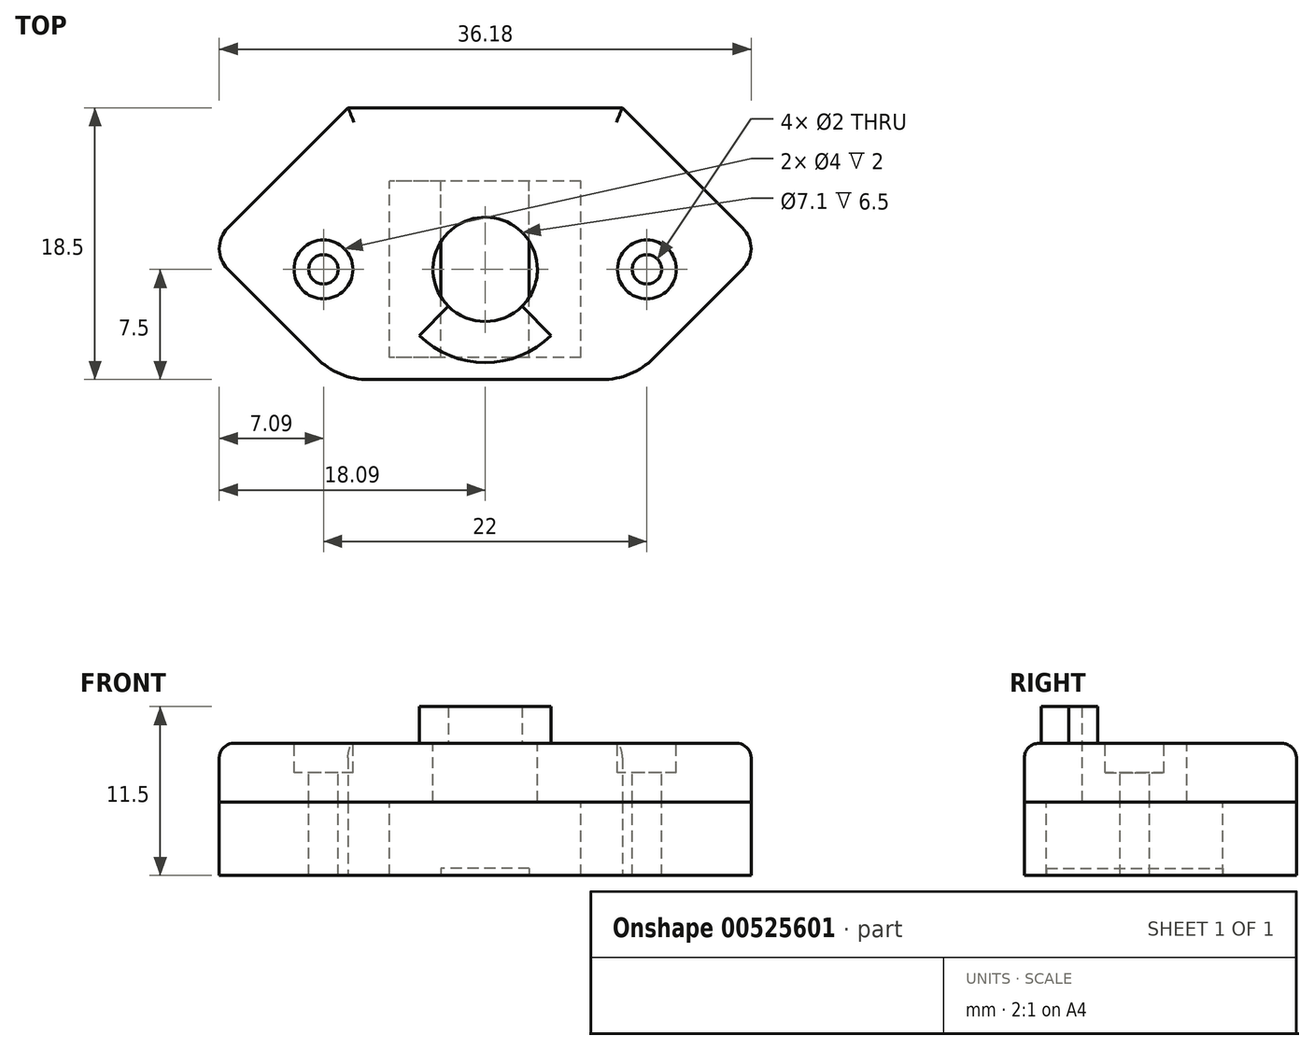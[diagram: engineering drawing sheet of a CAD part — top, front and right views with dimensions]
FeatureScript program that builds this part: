
annotation { "Feature Type Name" : "Feature", "Feature Type Description" : "" }
export const myFeature = defineFeature(function(context is Context, id is Id, definition is map)
    precondition{}
    {
        {
            var Q0;
            Q0=qCreatedBy(makeId("Top.planeOp"),FACE);
            var sketch = newSketch(context, id + "F0", { "sketchPlane" : qUnion([Q0])});
            skLineSegment(sketch, "E0.top", {"start": v(10, 15) * mm, "end": v(-10, 15) * mm});
            skLineSegment(sketch, "E0.left", {"start": v(10, 0) * mm, "end": v(10, 15) * mm});
            skLineSegment(sketch, "E0.right", {"start": v(-10, 0) * mm, "end": v(-10, 15) * mm});
            skPoint(sketch, "E0.middle", {"position": v(0, 7.5) * mm});
            skLineSegment(sketch, "E1", {"start": v(-10, 0) * mm, "end": v(10, 0) * mm});
            skLineSegment(sketch, "E2", {"start": v(0, 7.5) * mm, "end": v(-25.69, 7.5) * mm, "construction": true});
            skArc(sketch, "E3", {"start": v(-17.5, 7.5) * mm, "mid": v(-15.3, 2.2) * mm, "end": v(-10, 0) * mm, "construction": true});
            skLineSegment(sketch, "E4", {"start": v(-10, 0) * mm, "end": v(-17.5, 7.5) * mm});
            skLineSegment(sketch, "E5", {"start": v(-17.5, 7.5) * mm, "end": v(-10, 15) * mm});
            skLineSegment(sketch, "E6", {"start": v(-10, 15) * mm, "end": v(-6.5, 18.5) * mm});
            skLineSegment(sketch, "E7", {"start": v(-6.5, 18.5) * mm, "end": v(6.5, 18.5) * mm});
            skLineSegment(sketch, "E8", {"start": v(10, 0) * mm, "end": v(17.5, 7.5) * mm});
            skLineSegment(sketch, "E9", {"start": v(10, 15) * mm, "end": v(17.5, 7.5) * mm});
            skLineSegment(sketch, "E10", {"start": v(10, 15) * mm, "end": v(6.5, 18.5) * mm});
            skLineSegment(sketch, "E11", {"start": v(-17.5, 7.5) * mm, "end": v(-18.91, 8.91) * mm});
            skLineSegment(sketch, "E12", {"start": v(-18.91, 8.91) * mm, "end": v(-9.33, 18.5) * mm});
            skLineSegment(sketch, "E13", {"start": v(-9.33, 18.5) * mm, "end": v(-6.5, 18.5) * mm});
            skLineSegment(sketch, "E14", {"start": v(17.5, 7.5) * mm, "end": v(18.91, 8.91) * mm});
            skLineSegment(sketch, "E15", {"start": v(18.91, 8.91) * mm, "end": v(9.33, 18.5) * mm});
            skLineSegment(sketch, "E16", {"start": v(9.33, 18.5) * mm, "end": v(6.5, 18.5) * mm});
            skSolve(sketch);
        }
        {
            var Q0;
            Q0=qSketchRegion(id+"F0",true);
            extrude(context, id + "F1", {"entities" : qUnion([Q0]), "depth" : 5 * mm, "offsetDistance" : 25 * mm});
        }
        {
            var Q0;
            Q0=makeQuery(id+"F1.opExtrude","CAP_FACE",FACE,{"disambiguationData":[OSD([sQuery(id+"F0.wireOp",EDGE,"E1"),sQuery(id+"F0.wireOp",EDGE,"E4"),sQuery(id+"F0.wireOp",EDGE,"E5"),sQuery(id+"F0.wireOp",EDGE,"E6"),sQuery(id+"F0.wireOp",EDGE,"E7"),sQuery(id+"F0.wireOp",EDGE,"E8"),sQuery(id+"F0.wireOp",EDGE,"E9"),sQuery(id+"F0.wireOp",EDGE,"E10")])],"isStart":false});
            var sketch = newSketch(context, id + "F2", { "sketchPlane" : qUnion([Q0])});
            skCircle(sketch, "E17", {"center": v(-11, 7.5) * mm, "radius": 1 * mm});
            skCircle(sketch, "E18", {"center": v(11, 7.5) * mm, "radius": 1 * mm});
            skCircle(sketch, "E19", {"center": v(0, 7.5) * mm, "radius": 3.55 * mm, "construction": true});
            skLineSegment(sketch, "E20.bottom", {"start": v(6.5, 1.5) * mm, "end": v(-6.5, 1.5) * mm});
            skLineSegment(sketch, "E20.top", {"start": v(6.5, 13.5) * mm, "end": v(-6.5, 13.5) * mm});
            skLineSegment(sketch, "E20.left", {"start": v(6.5, 1.5) * mm, "end": v(6.5, 13.5) * mm});
            skLineSegment(sketch, "E20.right", {"start": v(-6.5, 1.5) * mm, "end": v(-6.5, 13.5) * mm});
            skSolve(sketch);
        }
        {
            var Q0;
            Q0=qSketchRegion(id+"F2",true);
            extrude(context, id + "F3", {"entities" : qUnion([Q0]), "operationType" : NewBodyOperationType.REMOVE, "oppositeDirection" : true, "offsetDistance" : 25 * mm, "depth" : 5 * mm});
        }
        {
            var Q0;
            Q0=makeQuery(id+"F1.opExtrude","CAP_FACE",FACE,{"disambiguationData":[OSD([sQuery(id+"F0.wireOp",EDGE,"E0.top"),sQuery(id+"F0.wireOp",EDGE,"6JZFKnFd-4U4Z-A5hn-TgZ8-hM0N97EqA9dV"),sQuery(id+"F0.wireOp",EDGE,"Ptp1BsVZ-AEQ3-b6oq-Bfdl-BXNrkdz5Nnmn"),sQuery(id+"F0.wireOp",EDGE,"E1")])],"isStart":true});
            var sketch = newSketch(context, id + "F4", { "sketchPlane" : qUnion([Q0])});
            skPoint(sketch, "E21.middle.positionSnap0", {"position": v(0, -13.5) * mm});
            skPoint(sketch, "E21.centerSnap0", {"position": v(0, -13.5) * mm});
            skLineSegment(sketch, "E22.bottom", {"start": v(3, -1.5) * mm, "end": v(-3, -1.5) * mm});
            skLineSegment(sketch, "E22.top", {"start": v(3, -13.5) * mm, "end": v(-3, -13.5) * mm});
            skLineSegment(sketch, "E22.left", {"start": v(3, -1.5) * mm, "end": v(3, -13.5) * mm});
            skLineSegment(sketch, "E22.right", {"start": v(-3, -1.5) * mm, "end": v(-3, -13.5) * mm});
            skPoint(sketch, "E22.middle", {"position": v(0, -7.5) * mm});
            skPoint(sketch, "E22.middle.positionSnap0", {"position": v(6.5, -7.5) * mm});
            skPoint(sketch, "E22.centerSnap0", {"position": v(6.5, -7.5) * mm});
            skSolve(sketch);
        }
        {
            var Q0;
            Q0 = qSketchRegion(id + "F4", true);
            extrude(context, id + "F5", {"entities" : qUnion([Q0]), "operationType" : NewBodyOperationType.ADD, "oppositeDirection" : true, "depth" : 0.5 * mm, "offsetDistance" : 25 * mm});
        }
        {
            var Q0;
            Q0=makeQuery(id+"F1.opExtrude","CAP_FACE",FACE,{"disambiguationData":[OSD([sQuery(id+"F0.wireOp",EDGE,"E0.top"),sQuery(id+"F0.wireOp",EDGE,"6JZFKnFd-4U4Z-A5hn-TgZ8-hM0N97EqA9dV"),sQuery(id+"F0.wireOp",EDGE,"Ptp1BsVZ-AEQ3-b6oq-Bfdl-BXNrkdz5Nnmn"),sQuery(id+"F0.wireOp",EDGE,"E1")])],"isStart":false});
            var sketch = newSketch(context, id + "F6", { "sketchPlane" : qUnion([Q0])});
            skLineSegment(sketch, "E23", {"start": v(-10, 0) * mm, "end": v(-18.91, 8.91) * mm});
            skLineSegment(sketch, "E24", {"start": v(-18.91, 8.91) * mm, "end": v(-9.33, 18.5) * mm});
            skLineSegment(sketch, "E25", {"start": v(-9.33, 18.5) * mm, "end": v(9.33, 18.5) * mm});
            skLineSegment(sketch, "E26", {"start": v(9.33, 18.5) * mm, "end": v(18.91, 8.91) * mm});
            skLineSegment(sketch, "E27", {"start": v(18.91, 8.91) * mm, "end": v(10, 0) * mm});
            skLineSegment(sketch, "E28", {"start": v(10, 0) * mm, "end": v(-10, 0) * mm});
            skSolve(sketch);
        }
        {
            var Q0;
            Q0 = qSketchRegion(id + "F6", true);
            extrude(context, id + "F7", {"entities" : qUnion([Q0]), "depth" : 4 * mm, "offsetDistance" : 25 * mm});
        }
        {
            var Q0;
            Q0=makeQuery(id+"F7.opExtrude","CAP_FACE",FACE,{"disambiguationData":[OSD([sQuery(id+"F6.wireOp",EDGE,"E23"),sQuery(id+"F6.wireOp",EDGE,"E24"),sQuery(id+"F6.wireOp",EDGE,"E25"),sQuery(id+"F6.wireOp",EDGE,"E26"),sQuery(id+"F6.wireOp",EDGE,"E27"),sQuery(id+"F6.wireOp",EDGE,"E28")])],"isStart":false});
            var sketch = newSketch(context, id + "F8", { "sketchPlane" : qUnion([Q0])});
            skCircle(sketch, "E29", {"center": v(-11, 7.5) * mm, "radius": 1 * mm, "construction": true});
            skCircle(sketch, "E30", {"center": v(11, 7.5) * mm, "radius": 1 * mm, "construction": true});
            skCircle(sketch, "E31", {"center": v(0, 7.5) * mm, "radius": 3.55 * mm});
            skLineSegment(sketch, "E32", {"start": v(0, 7.5) * mm, "end": v(-2.51, 4.99) * mm, "construction": true});
            skLineSegment(sketch, "E33", {"start": v(0, 7.5) * mm, "end": v(2.08, 7.5) * mm, "construction": true});
            skLineSegment(sketch, "E34", {"start": v(0, 8.49) * mm, "end": v(0, 7.5) * mm, "construction": true});
            skLineSegment(sketch, "E35", {"start": v(0, 7.5) * mm, "end": v(2.51, 4.99) * mm, "construction": true});
            skLineSegment(sketch, "E36", {"start": v(-2.51, 4.99) * mm, "end": v(-3.57, 3.93) * mm, "construction": true});
            skLineSegment(sketch, "E37", {"start": v(2.51, 4.99) * mm, "end": v(3.57, 3.93) * mm, "construction": true});
            skArc(sketch, "E38", {"start": v(-3.57, 3.93) * mm, "mid": v(0, 2.45) * mm, "end": v(3.57, 3.93) * mm, "construction": true});
            skSolve(sketch);
        }
        {
            var Q0;
            Q0 = qSketchRegion(id + "F8", true);
            extrude(context, id + "F9", {"entities" : qUnion([Q0]), "operationType" : NewBodyOperationType.REMOVE, "oppositeDirection" : true, "depth" : 4 * mm, "offsetDistance" : 25 * mm});
        }
        {
            var Q0;
            Q0=makeQuery(id+"F7.opExtrude","CAP_EDGE",EDGE,{"disambiguationData":[OSD([sQuery(id+"F6.wireOp",EDGE,"E23")])],"isStart":false});
            var Q1;
            Q1=makeQuery(id+"F7.opExtrude","CAP_EDGE",EDGE,{"disambiguationData":[OSD([sQuery(id+"F6.wireOp",EDGE,"E28")])],"isStart":false});
            var Q2;
            Q2=makeQuery(id+"F7.opExtrude","CAP_EDGE",EDGE,{"disambiguationData":[OSD([sQuery(id+"F6.wireOp",EDGE,"E27")])],"isStart":false});
            var Q3;
            Q3=makeQuery(id+"F7.opExtrude","CAP_EDGE",EDGE,{"disambiguationData":[OSD([sQuery(id+"F6.wireOp",EDGE,"E26")])],"isStart":false});
            var Q4;
            Q4=makeQuery(id+"F7.opExtrude","CAP_EDGE",EDGE,{"disambiguationData":[OSD([sQuery(id+"F6.wireOp",EDGE,"E25")])],"isStart":false});
            var Q5;
            Q5=makeQuery(id+"F7.opExtrude","CAP_EDGE",EDGE,{"disambiguationData":[OSD([sQuery(id+"F6.wireOp",EDGE,"E24")])],"isStart":false});
            fillet(context, id + "F10", {"entities" : qUnion([Q0, Q1, Q2, Q3, Q4, Q5]), "radius" : 1 * mm, "tangentPropagation" : true, "defaultsChanged" : false, "vertexSettings" : [], "allowEdgeOverflow" : false});
        }
        {
            var Q0;
            Q0=sQuery(id+"F8.wireOp",VERTEX,"E30.center");
            var Q1;
            Q1=sQuery(id+"F8.wireOp",VERTEX,"E29.center");
            var Q2;
            Q2=makeQuery(id+"F7.opExtrude","SWEPT_BODY",BODY,{"disambiguationData":[OSD([sQuery(id+"F6.wireOp",EDGE,"E23"),sQuery(id+"F6.wireOp",EDGE,"E24"),sQuery(id+"F6.wireOp",EDGE,"E25"),sQuery(id+"F6.wireOp",EDGE,"E26"),sQuery(id+"F6.wireOp",EDGE,"E27"),sQuery(id+"F6.wireOp",EDGE,"E28")])]});
            hole(context, id + "F11", {"style" : HoleStyle.C_BORE, "endStyle" : HoleEndStyle.BLIND, "holeDiameter" : 2 * mm, "cBoreDiameter" : 4 * mm, "cBoreDepth" : 2 * mm, "majorDiameter" : 5 * mm, "holeDepth" : 20 * mm, "tappedDepth" : 12 * mm, "tapClearance" : 3, "locations" : qUnion([Q0, Q1]), "scope" : qUnion([Q2])});
        }
        {
            var Q0;
            Q0=makeQuery(id+"F1.opExtrude","SWEPT_EDGE",EDGE,{"disambiguationData":[OSD([sQuery(id+"F0.wireOp",EDGE,"E0.right"),sQuery(id+"F0.wireOp",EDGE,"E1"),sQuery(id+"F0.wireOp",EDGE,"E4")])]});
            var Q1;
            Q1=makeQuery(id+"F1.opExtrude","SWEPT_EDGE",EDGE,{"disambiguationData":[OSD([sQuery(id+"F0.wireOp",EDGE,"E6"),sQuery(id+"F0.wireOp",EDGE,"E7")])]});
            var Q2;
            Q2=makeQuery(id+"F1.opExtrude","SWEPT_EDGE",EDGE,{"disambiguationData":[OSD([sQuery(id+"F0.wireOp",EDGE,"E0.left"),sQuery(id+"F0.wireOp",EDGE,"E1"),sQuery(id+"F0.wireOp",EDGE,"E8")])]});
            var Q3;
            Q3=makeQuery(id+"F1.opExtrude","SWEPT_EDGE",EDGE,{"disambiguationData":[OSD([sQuery(id+"F0.wireOp",EDGE,"E7"),sQuery(id+"F0.wireOp",EDGE,"E10")])]});
            fillet(context, id + "F12", {"entities" : qUnion([Q0, Q1, Q2, Q3]), "tangentPropagation" : true, "radius" : 5 * mm, "defaultsChanged" : false, "vertexSettings" : [], "allowEdgeOverflow" : false});
        }
        {
            var Q0;
            Q0=makeQuery(id+"F1.opExtrude","SWEPT_EDGE",EDGE,{"disambiguationData":[OSD([sQuery(id+"F0.wireOp",EDGE,"E11"),sQuery(id+"F0.wireOp",EDGE,"E12")])]});
            var Q1;
            Q1=makeQuery(id+"F1.opExtrude","SWEPT_EDGE",EDGE,{"disambiguationData":[OSD([sQuery(id+"F0.wireOp",EDGE,"E14"),sQuery(id+"F0.wireOp",EDGE,"E15")])]});
            fillet(context, id + "F13", {"entities" : qUnion([Q0, Q1]), "tangentPropagation" : true, "radius" : 2 * mm, "defaultsChanged" : false, "vertexSettings" : [], "allowEdgeOverflow" : false});
        }
        {
            var Q0;
            Q0=makeQuery(id+"F7.opExtrude","SWEPT_EDGE",EDGE,{"disambiguationData":[OSD([sQuery(id+"F6.wireOp",EDGE,"E23"),sQuery(id+"F6.wireOp",EDGE,"E28")])]});
            var Q1;
            Q1=makeQuery(id+"F7.opExtrude","SWEPT_EDGE",EDGE,{"disambiguationData":[OSD([sQuery(id+"F6.wireOp",EDGE,"E27"),sQuery(id+"F6.wireOp",EDGE,"E28")])]});
            fillet(context, id + "F14", {"entities" : qUnion([Q0, Q1]), "tangentPropagation" : true, "radius" : 5 * mm, "defaultsChanged" : false, "vertexSettings" : [], "allowEdgeOverflow" : false});
        }
        {
            var Q0;
            Q0=makeQuery(id+"F7.opExtrude","SWEPT_EDGE",EDGE,{"disambiguationData":[OSD([sQuery(id+"F6.wireOp",EDGE,"E23"),sQuery(id+"F6.wireOp",EDGE,"E24")])]});
            var Q1;
            Q1=makeQuery(id+"F7.opExtrude","SWEPT_EDGE",EDGE,{"disambiguationData":[OSD([sQuery(id+"F6.wireOp",EDGE,"E26"),sQuery(id+"F6.wireOp",EDGE,"E27")])]});
            fillet(context, id + "F15", {"entities" : qUnion([Q0, Q1]), "tangentPropagation" : true, "radius" : 2 * mm, "defaultsChanged" : false, "vertexSettings" : [], "allowEdgeOverflow" : false});
        }
        {
            var Q0;
            Q0=makeQuery(id+"F7.opExtrude","CAP_FACE",FACE,{"disambiguationData":[OSD([sQuery(id+"F6.wireOp",EDGE,"E23"),sQuery(id+"F6.wireOp",EDGE,"E24"),sQuery(id+"F6.wireOp",EDGE,"E25"),sQuery(id+"F6.wireOp",EDGE,"E26"),sQuery(id+"F6.wireOp",EDGE,"E27"),sQuery(id+"F6.wireOp",EDGE,"E28")])],"isStart":false});
            var sketch = newSketch(context, id + "F16", { "sketchPlane" : qUnion([Q0])});
            skLineSegment(sketch, "E39", {"start": v(0, 7.5) * mm, "end": v(-2.51, 4.99) * mm, "construction": true});
            skLineSegment(sketch, "E40", {"start": v(0, 7.5) * mm, "end": v(0, 6.34) * mm, "construction": true});
            skLineSegment(sketch, "E41", {"start": v(0, 7.5) * mm, "end": v(2.51, 4.99) * mm, "construction": true});
            skLineSegment(sketch, "E42", {"start": v(-2.51, 4.99) * mm, "end": v(-4.5, 3) * mm, "construction": true});
            skLineSegment(sketch, "E43", {"start": v(2.51, 4.99) * mm, "end": v(4.5, 3) * mm, "construction": true});
            skArc(sketch, "E44", {"start": v(-4.5, 3) * mm, "mid": v(0, 1.15) * mm, "end": v(4.5, 3) * mm});
            skArc(sketch, "E45", {"start": v(-2.51, 4.99) * mm, "mid": v(0, 3.95) * mm, "end": v(2.51, 4.99) * mm});
            skLineSegment(sketch, "E46", {"start": v(-2.51, 4.99) * mm, "end": v(-4.5, 3) * mm});
            skLineSegment(sketch, "E47", {"start": v(2.51, 4.99) * mm, "end": v(4.5, 3) * mm});
            skSolve(sketch);
        }
        {
            var Q0;
            Q0 = qSketchRegion(id + "F16", true);
            extrude(context, id + "F17", {"entities" : qUnion([Q0]), "operationType" : NewBodyOperationType.ADD, "depth" : 2.5 * mm, "offsetDistance" : 25 * mm});
        }
    });
